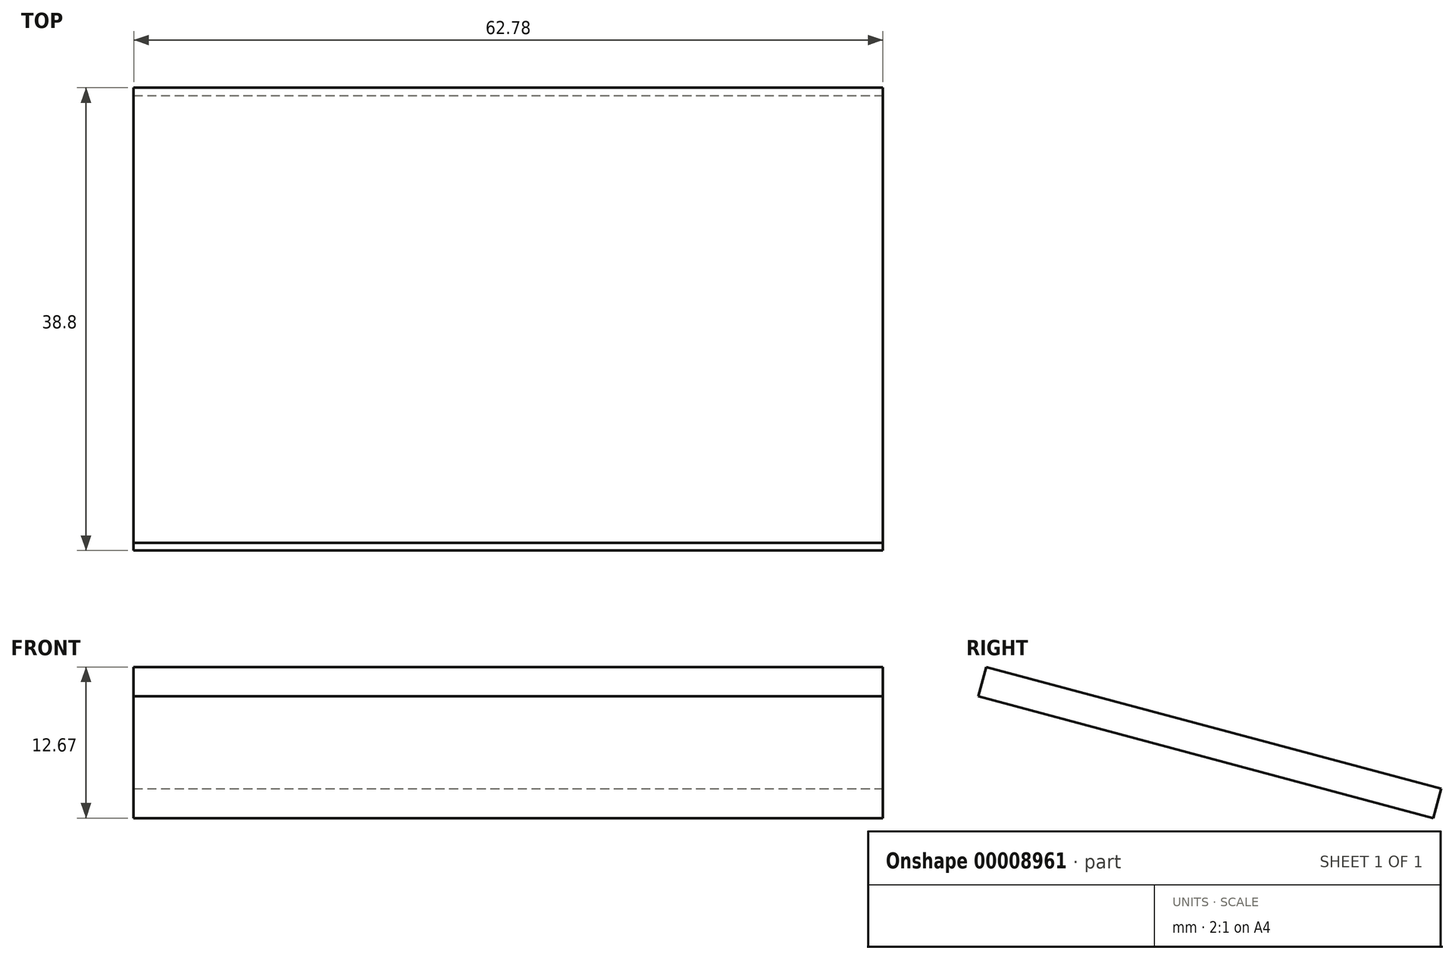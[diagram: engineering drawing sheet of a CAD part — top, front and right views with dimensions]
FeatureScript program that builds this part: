
annotation { "Feature Type Name" : "Feature", "Feature Type Description" : "" }
export const myFeature = defineFeature(function(context is Context, id is Id, definition is map)
    precondition{}
    {
        {
            var Q0;
            Q0=qCreatedBy(makeId("Top.planeOp"),FACE);
            var sketch = newSketch(context, id + "F0", { "sketchPlane" : qUnion([Q0])});
            skLineSegment(sketch, "E0", {"start": v(-60.04, 0) * mm, "end": v(45.5, 0) * mm, "construction": true});
            skSolve(sketch);
        }
        {
            var Q0;
            Q0=sQuery(id+"F0.wireOp",EDGE,"E0");
            cPlane(context, id + "F1", {"entities" : qUnion([Q0]), "cplaneType" : CPlaneType.LINE_ANGLE, "offset" : 152.4 * mm, "angle" : 75 * degree, "width" : 152.4 * mm, "height" : 152.4 * mm});
        }
        {
            var Q0;
            Q0=qCreatedBy(id+"F1.planeOp",FACE);
            var sketch = newSketch(context, id + "F2", { "sketchPlane" : qUnion([Q0])});
            skLineSegment(sketch, "E1.bottom", {"start": v(-38.61, -8.6) * mm, "end": v(24.17, -8.6) * mm});
            skLineSegment(sketch, "E1.top", {"start": v(-38.61, 30.88) * mm, "end": v(24.17, 30.88) * mm});
            skLineSegment(sketch, "E1.left", {"start": v(-38.61, -8.6) * mm, "end": v(-38.61, 30.88) * mm});
            skLineSegment(sketch, "E1.right", {"start": v(24.17, -8.6) * mm, "end": v(24.17, 30.88) * mm});
            skLineSegment(sketch, "E2", {"start": v(0, -24.53) * mm, "end": v(0, 43.45) * mm, "construction": true});
            skSolve(sketch);
        }
        {
            var Q0;
            Q0=makeQuery(id+"F2.imprint","IMPRINT",FACE,{"disambiguationData":[TD([[makeQuery(id+"F2.imprint","IMPRINT",EDGE,{"derivedFrom":sQuery(id+"F2.wireOp",EDGE,"E1.bottom")}),1.0]])]});
            extrude(context, id + "F3", {"entities" : qUnion([Q0]), "depth" : 2.54 * mm});
        }
    });
